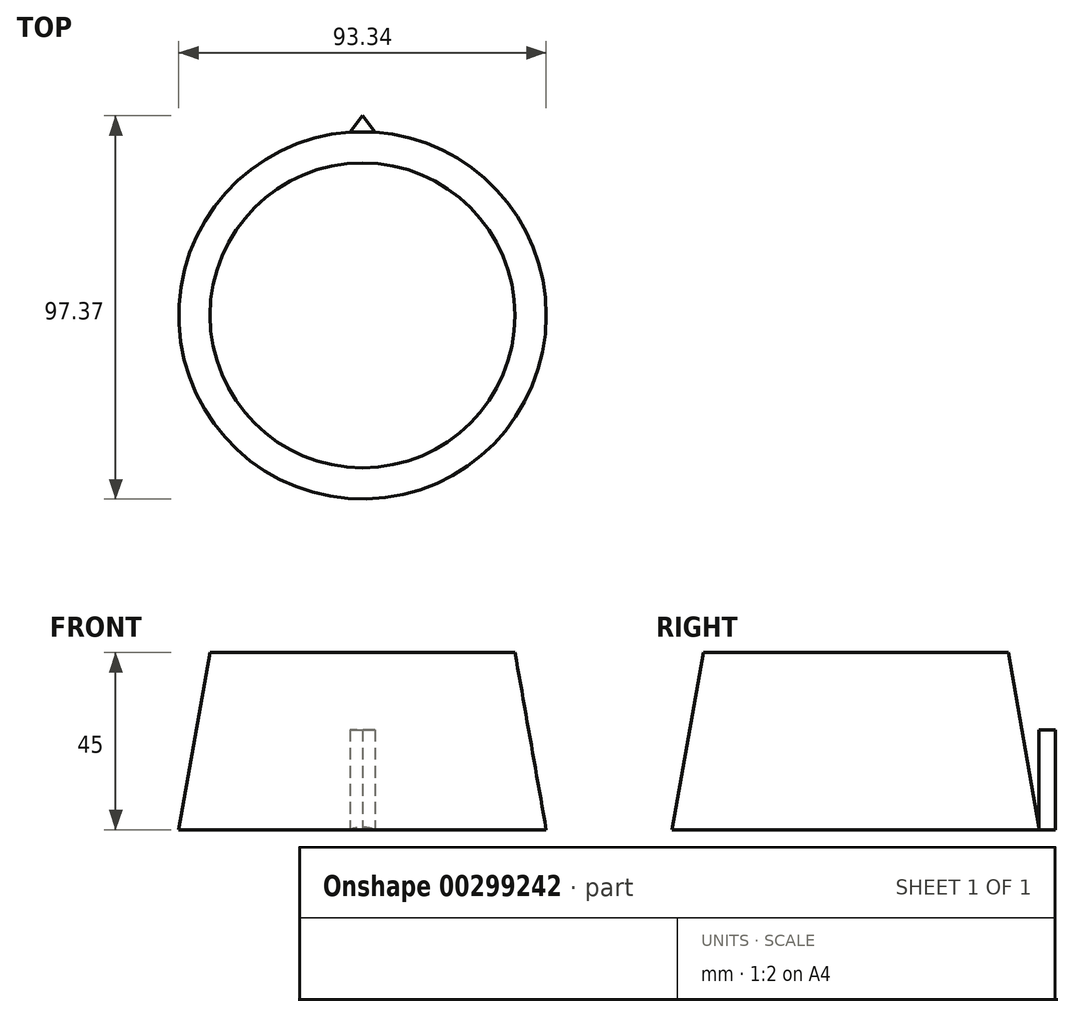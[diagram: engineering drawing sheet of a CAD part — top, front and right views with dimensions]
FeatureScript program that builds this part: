
annotation { "Feature Type Name" : "Feature", "Feature Type Description" : "" }
export const myFeature = defineFeature(function(context is Context, id is Id, definition is map)
    precondition{}
    {
        {
            var Q0;
            Q0=qCreatedBy(makeId("Top.planeOp"),FACE);
            var sketch = newSketch(context, id + "F0", { "sketchPlane" : qUnion([Q0])});
            skCircle(sketch, "E0", {"center": v(0, 0) * mm, "radius": 46.67 * mm});
            skSolve(sketch);
        }
        {
            var Q0;
            Q0 = qSketchRegion(id + "F0", true);
            extrude(context, id + "F1", {"entities" : qUnion([Q0]), "depth" : 45 * mm, "hasDraft" : true, "draftAngle" : 10 * degree, "draftPullDirection" : true});
        }
        {
            var Q0;
            Q0=qCreatedBy(makeId("Top.planeOp"),FACE);
            var sketch = newSketch(context, id + "F2", { "sketchPlane" : qUnion([Q0])});
            skLineSegment(sketch, "E1", {"start": v(-3.15, 46.56) * mm, "end": v(0, 50.7) * mm});
            skLineSegment(sketch, "E2", {"start": v(0, 50.7) * mm, "end": v(3.15, 46.56) * mm});
            skLineSegment(sketch, "E3", {"start": v(3.15, 46.56) * mm, "end": v(-3.15, 46.56) * mm});
            skSolve(sketch);
        }
        {
            var Q0;
            Q0=qCreatedBy(makeId("Top.planeOp"),FACE);
            var sketch = newSketch(context, id + "F3", { "sketchPlane" : qUnion([Q0])});
            skLineSegment(sketch, "E4", {"start": v(3.17, 39.14) * mm, "end": v(3.17, 47.2) * mm});
            skLineSegment(sketch, "E5", {"start": v(-4.32, 39.43) * mm, "end": v(-4.32, 46.62) * mm});
            skSolve(sketch);
        }
        {
            var Q0;
            Q0 = qSketchRegion(id + "F3", true);
            var Q1;
            Q1=makeQuery(id+"F2.imprint","IMPRINT",FACE,{"disambiguationData":[TD([[makeQuery(id+"F2.imprint","IMPRINT",EDGE,{"derivedFrom":sQuery(id+"F2.wireOp",EDGE,"E1")}),-1.0]])]});
            extrude(context, id + "F4", {"entities" : qUnion([Q0, Q1]), "operationType" : NewBodyOperationType.ADD, "depth" : 25.4 * mm});
        }
    });
